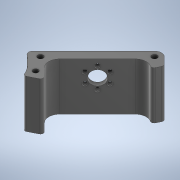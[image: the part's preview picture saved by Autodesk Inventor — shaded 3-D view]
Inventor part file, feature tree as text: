
AUTODESK INVENTOR PART (.ipt)
format: ipt  version: 2020 (Build 240168000, 168)  size: 668,160 bytes
history: native  units: mm
features: extrude x6, sketch x5, other x1, chamfer x1, fillet x1, projected_geometry x1
ambient origin geometry x8: Origin, YZ Plane, XZ Plane, XY Plane, X Axis, Y Axis, Z Axis, Center Point
bodies: Body1 (feature_tree)
feature tree (15):
  other  "Твердое тело1"
  sketch  "Эскиз1"
  extrude  "Выдавливание10"  Depth=4.0mm
  sketch  "Эскиз6"
  extrude  "Выдавливание13"  Depth=6.0mm
  extrude  "Выдавливание14"  Depth=35.0mm TaperAngle=0.0deg
  chamfer  "Фаска3"  Distance=59.0mm
  extrude  "Выдавливание15"  Depth=21.2mm
  fillet  "Сопряжение1"  Radius=15.0mm
  extrude  "Выдавливание16"  Depth=10.4mm
  extrude  "Выдавливание17"  Depth=2.5mm
  sketch  "Эскиз7"
  sketch  "Эскиз8"
  projected_geometry  "Спроецированная петля3"
  sketch  "Эскиз9"
